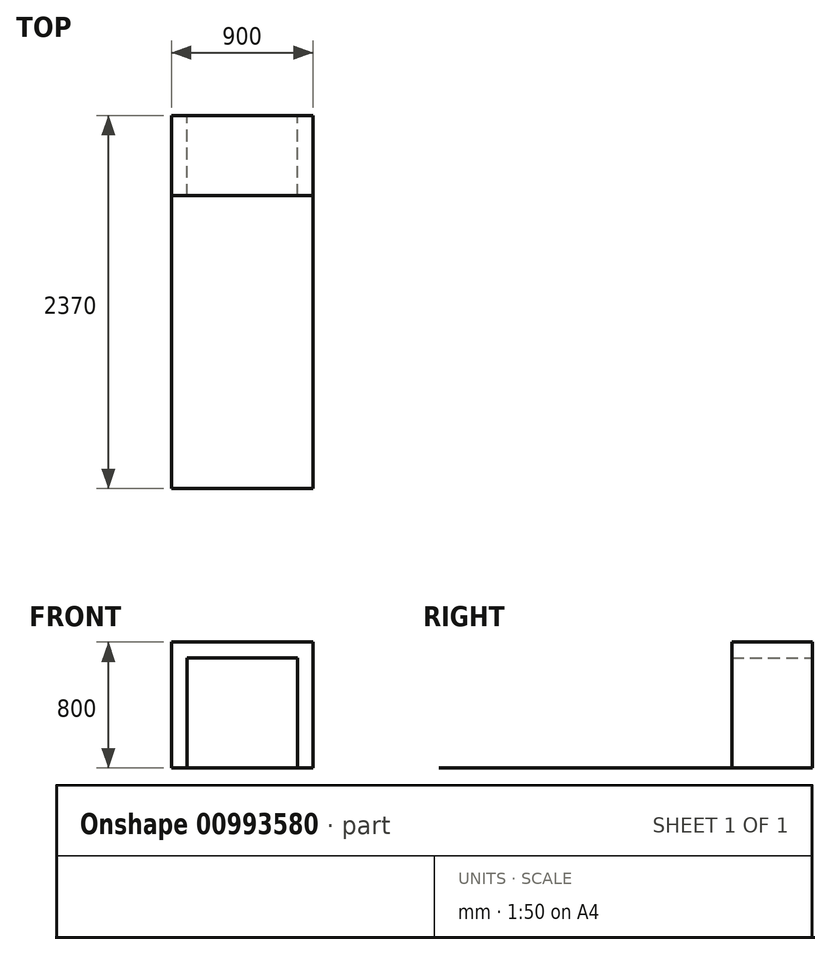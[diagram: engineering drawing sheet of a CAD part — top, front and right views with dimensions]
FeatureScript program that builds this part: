
annotation { "Feature Type Name" : "Feature", "Feature Type Description" : "" }
export const myFeature = defineFeature(function(context is Context, id is Id, definition is map)
    precondition{}
    {
        {
            var Q0;
            Q0=qCreatedBy(makeId("Front.planeOp"),FACE);
            var sketch = newSketch(context, id + "F0", { "sketchPlane" : qUnion([Q0])});
            skLineSegment(sketch, "E0", {"start": v(0, 0) * mm, "end": v(0, 1402.45) * mm, "construction": true});
            skLineSegment(sketch, "E1", {"start": v(0, 800) * mm, "end": v(-450, 800) * mm});
            skLineSegment(sketch, "E2", {"start": v(-450, 800) * mm, "end": v(-450, 0) * mm});
            skLineSegment(sketch, "E3", {"start": v(-450, 0) * mm, "end": v(-350, 0) * mm});
            skLineSegment(sketch, "E4", {"start": v(-350, 0) * mm, "end": v(-350, 700) * mm});
            skLineSegment(sketch, "E5", {"start": v(-350, 700) * mm, "end": v(0, 700) * mm});
            skLineSegment(sketch, "E6", {"start": v(0, 0) * mm, "end": v(-350, 0) * mm, "construction": true});
            skLineSegment(sketch, "E7.MirrorCS", {"start": v(0, 800) * mm, "end": v(450, 800) * mm});
            skLineSegment(sketch, "E8.MirrorCS", {"start": v(450, 0) * mm, "end": v(350, 0) * mm});
            skLineSegment(sketch, "E9.MirrorCS", {"start": v(0, 0) * mm, "end": v(350, 0) * mm, "construction": true});
            skLineSegment(sketch, "E10.MirrorCS", {"start": v(350, 700) * mm, "end": v(0, 700) * mm});
            skLineSegment(sketch, "E11.MirrorCS", {"start": v(450, 800) * mm, "end": v(450, 0) * mm});
            skLineSegment(sketch, "E12.MirrorCS", {"start": v(350, 0) * mm, "end": v(350, 700) * mm});
            skSolve(sketch);
        }
        {
            var Q0;
            Q0=makeQuery(id+"F0.imprint","IMPRINT",FACE,{"disambiguationData":[TD([[makeQuery(id+"F0.imprint","IMPRINT",EDGE,{"derivedFrom":sQuery(id+"F0.wireOp",EDGE,"E1")}),1.0]])]});
            extrude(context, id + "F1", {"entities" : qUnion([Q0]), "depth" : 510 * mm, "offsetDistance" : 25 * mm});
        }
        {
            var Q0;
            Q0=qCreatedBy(makeId("Front.planeOp"),FACE);
            var sketch = newSketch(context, id + "F2", { "sketchPlane" : qUnion([Q0])});
            skLineSegment(sketch, "E13", {"start": v(0, 0) * mm, "end": v(-450, 0) * mm});
            skLineSegment(sketch, "E14", {"start": v(-450, 0) * mm, "end": v(-450, 1) * mm});
            skLineSegment(sketch, "E15", {"start": v(-450, 1) * mm, "end": v(450, 1) * mm});
            skLineSegment(sketch, "E16", {"start": v(450, 1) * mm, "end": v(450, 0) * mm});
            skLineSegment(sketch, "E17", {"start": v(450, 0) * mm, "end": v(0, 0) * mm});
            skSolve(sketch);
        }
        {
            var Q0;
            Q0 = qSketchRegion(id + "F2", true);
            extrude(context, id + "F3", {"entities" : qUnion([Q0]), "operationType" : NewBodyOperationType.ADD, "depth" : 2370 * mm, "offsetDistance" : 25 * mm});
        }
    });
